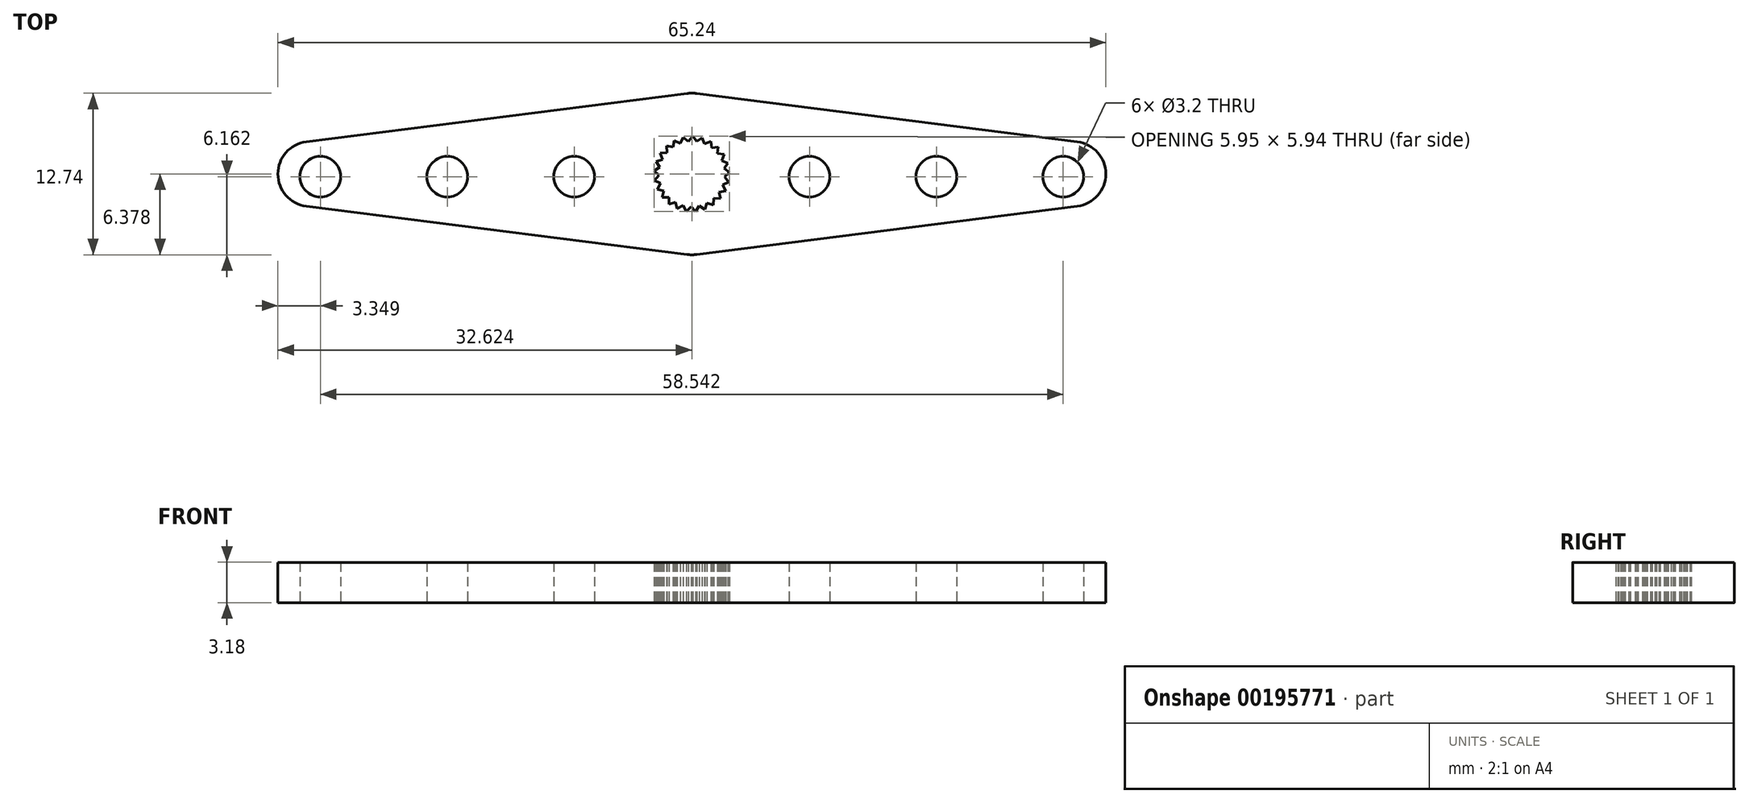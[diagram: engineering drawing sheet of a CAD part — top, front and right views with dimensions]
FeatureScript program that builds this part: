
annotation { "Feature Type Name" : "Feature", "Feature Type Description" : "" }
export const myFeature = defineFeature(function(context is Context, id is Id, definition is map)
    precondition{}
    {
        {
            var Q0;
            Q0=qCreatedBy(makeId("Top.planeOp"),FACE);
            var sketch = newSketch(context, id + "F0", { "sketchPlane" : qUnion([Q0])});
            skLineSegment(sketch, "E0", {"start": v(-2.48, 1.65) * mm, "end": v(-2.31, 1.15) * mm});
            skLineSegment(sketch, "E1", {"start": v(-2.31, 1.15) * mm, "end": v(-2.81, 0.98) * mm});
            skLineSegment(sketch, "E2.1.0", {"start": v(-2.81, 0.98) * mm, "end": v(-2.53, 0.54) * mm});
            skLineSegment(sketch, "E2.1.1", {"start": v(-2.53, 0.54) * mm, "end": v(-2.97, 0.25) * mm});
            skLineSegment(sketch, "E2.2.0", {"start": v(-2.97, 0.25) * mm, "end": v(-2.58, -0.1) * mm});
            skLineSegment(sketch, "E2.2.1", {"start": v(-2.58, -0.1) * mm, "end": v(-2.94, -0.5) * mm});
            skLineSegment(sketch, "E2.3.0", {"start": v(-2.94, -0.5) * mm, "end": v(-2.47, -0.74) * mm});
            skLineSegment(sketch, "E2.3.1", {"start": v(-2.47, -0.74) * mm, "end": v(-2.72, -1.2) * mm});
            skLineSegment(sketch, "E2.4.0", {"start": v(-2.72, -1.2) * mm, "end": v(-2.21, -1.34) * mm});
            skLineSegment(sketch, "E2.4.1", {"start": v(-2.21, -1.34) * mm, "end": v(-2.34, -1.85) * mm});
            skLineSegment(sketch, "E2.5.0", {"start": v(-2.34, -1.85) * mm, "end": v(-1.8, -1.84) * mm});
            skLineSegment(sketch, "E2.5.1", {"start": v(-1.8, -1.84) * mm, "end": v(-1.8, -2.37) * mm});
            skLineSegment(sketch, "E2.6.0", {"start": v(-1.8, -2.37) * mm, "end": v(-1.3, -2.24) * mm});
            skLineSegment(sketch, "E2.6.1", {"start": v(-1.3, -2.24) * mm, "end": v(-1.16, -2.75) * mm});
            skLineSegment(sketch, "E2.7.0", {"start": v(-1.16, -2.75) * mm, "end": v(-0.7, -2.49) * mm});
            skLineSegment(sketch, "E2.7.1", {"start": v(-0.7, -2.49) * mm, "end": v(-0.44, -2.95) * mm});
            skLineSegment(sketch, "E2.8.0", {"start": v(-0.44, -2.95) * mm, "end": v(-0.06, -2.58) * mm});
            skLineSegment(sketch, "E2.8.1", {"start": v(-0.06, -2.58) * mm, "end": v(0.3, -2.96) * mm});
            skLineSegment(sketch, "E2.9.0", {"start": v(0.3, -2.96) * mm, "end": v(0.59, -2.52) * mm});
            skLineSegment(sketch, "E2.9.1", {"start": v(0.59, -2.52) * mm, "end": v(1.04, -2.8) * mm});
            skLineSegment(sketch, "E2.10.0", {"start": v(1.04, -2.8) * mm, "end": v(1.2, -2.3) * mm});
            skLineSegment(sketch, "E2.10.1", {"start": v(1.2, -2.3) * mm, "end": v(1.7, -2.45) * mm});
            skLineSegment(sketch, "E2.11.0", {"start": v(1.7, -2.45) * mm, "end": v(1.73, -1.92) * mm});
            skLineSegment(sketch, "E2.11.1", {"start": v(1.73, -1.92) * mm, "end": v(2.25, -1.95) * mm});
            skLineSegment(sketch, "E2.12.0", {"start": v(2.25, -1.95) * mm, "end": v(2.15, -1.43) * mm});
            skLineSegment(sketch, "E2.12.1", {"start": v(2.15, -1.43) * mm, "end": v(2.67, -1.33) * mm});
            skLineSegment(sketch, "E2.13.0", {"start": v(2.67, -1.33) * mm, "end": v(2.44, -0.85) * mm});
            skLineSegment(sketch, "E2.13.1", {"start": v(2.44, -0.85) * mm, "end": v(2.91, -0.62) * mm});
            skLineSegment(sketch, "E2.14.0", {"start": v(2.91, -0.62) * mm, "end": v(2.57, -0.22) * mm});
            skLineSegment(sketch, "E2.14.1", {"start": v(2.57, -0.22) * mm, "end": v(2.98, 0.12) * mm});
            skLineSegment(sketch, "E2.15.0", {"start": v(2.98, 0.12) * mm, "end": v(2.55, 0.43) * mm});
            skLineSegment(sketch, "E2.15.1", {"start": v(2.55, 0.43) * mm, "end": v(2.85, 0.86) * mm});
            skLineSegment(sketch, "E2.16.0", {"start": v(2.85, 0.86) * mm, "end": v(2.36, 1.05) * mm});
            skLineSegment(sketch, "E2.16.1", {"start": v(2.36, 1.05) * mm, "end": v(2.55, 1.54) * mm});
            skLineSegment(sketch, "E2.17.0", {"start": v(2.55, 1.54) * mm, "end": v(2.03, 1.6) * mm});
            skLineSegment(sketch, "E2.17.1", {"start": v(2.03, 1.6) * mm, "end": v(2.09, 2.13) * mm});
            skLineSegment(sketch, "E2.18.0", {"start": v(2.09, 2.13) * mm, "end": v(1.56, 2.06) * mm});
            skLineSegment(sketch, "E2.18.1", {"start": v(1.56, 2.06) * mm, "end": v(1.5, 2.58) * mm});
            skLineSegment(sketch, "E2.19.0", {"start": v(1.5, 2.58) * mm, "end": v(1, 2.38) * mm});
            skLineSegment(sketch, "E2.19.1", {"start": v(1, 2.38) * mm, "end": v(0.8, 2.87) * mm});
            skLineSegment(sketch, "E2.20.0", {"start": v(0.8, 2.87) * mm, "end": v(0.38, 2.56) * mm});
            skLineSegment(sketch, "E2.20.1", {"start": v(0.38, 2.56) * mm, "end": v(0.07, 2.98) * mm});
            skLineSegment(sketch, "E2.21.0", {"start": v(0.07, 2.98) * mm, "end": v(-0.27, 2.57) * mm});
            skLineSegment(sketch, "E2.21.1", {"start": v(-0.27, 2.57) * mm, "end": v(-0.68, 2.9) * mm});
            skLineSegment(sketch, "E2.22.0", {"start": v(-0.68, 2.9) * mm, "end": v(-0.9, 2.42) * mm});
            skLineSegment(sketch, "E2.22.1", {"start": v(-0.9, 2.42) * mm, "end": v(-1.38, 2.64) * mm});
            skLineSegment(sketch, "E2.23.0", {"start": v(-1.38, 2.64) * mm, "end": v(-1.47, 2.12) * mm});
            skLineSegment(sketch, "E2.23.1", {"start": v(-1.47, 2.12) * mm, "end": v(-2, 2.22) * mm});
            skLineSegment(sketch, "E2.24.0", {"start": v(-2, 2.22) * mm, "end": v(-1.95, 1.69) * mm});
            skLineSegment(sketch, "E2.24.1", {"start": v(-1.95, 1.69) * mm, "end": v(-2.48, 1.65) * mm});
            skPoint(sketch, "E2.center", {"position": v(0, 0) * mm});
            skLineSegment(sketch, "E3", {"start": v(-0.38, 6.35) * mm, "end": v(-30.38, 2.54) * mm});
            skLineSegment(sketch, "E4", {"start": v(-0.38, -6.35) * mm, "end": v(-30.38, -2.54) * mm});
            skArc(sketch, "E5", {"start": v(-30.38, 2.54) * mm, "mid": v(-32.62, 0) * mm, "end": v(-30.38, -2.54) * mm});
            skCircle(sketch, "E6", {"center": v(-9.27, -0.2) * mm, "radius": 1.6 * mm});
            skCircle(sketch, "E7", {"center": v(-19.27, -0.2) * mm, "radius": 1.6 * mm});
            skCircle(sketch, "E8", {"center": v(-29.27, -0.2) * mm, "radius": 1.6 * mm});
            skLineSegment(sketch, "E9.MirrorCS", {"start": v(0.38, 6.35) * mm, "end": v(30.38, 2.54) * mm});
            skLineSegment(sketch, "E10.MirrorCS", {"start": v(0.38, -6.35) * mm, "end": v(30.38, -2.54) * mm});
            skCircle(sketch, "E11.MirrorC", {"center": v(9.27, -0.2) * mm, "radius": 1.6 * mm});
            skCircle(sketch, "E12.MirrorC", {"center": v(19.27, -0.2) * mm, "radius": 1.6 * mm});
            skCircle(sketch, "E13.MirrorC", {"center": v(29.27, -0.2) * mm, "radius": 1.6 * mm});
            skArc(sketch, "E14.MirrorCS", {"start": v(30.38, 2.54) * mm, "mid": v(32.62, 0) * mm, "end": v(30.38, -2.54) * mm});
            skArc(sketch, "E15", {"start": v(0.38, 6.35) * mm, "mid": v(0, 6.37) * mm, "end": v(-0.38, 6.35) * mm});
            skArc(sketch, "E16", {"start": v(-0.38, -6.35) * mm, "mid": v(0, -6.37) * mm, "end": v(0.38, -6.35) * mm});
            skSolve(sketch);
        }
        {
            var Q0;
            Q0=makeQuery(id+"F0.imprint","IMPRINT",FACE,{"disambiguationData":[TD([[makeQuery(id+"F0.imprint","IMPRINT",EDGE,{"derivedFrom":sQuery(id+"F0.wireOp",EDGE,"E0")}),-1.0]])]});
            extrude(context, id + "F1", {"entities" : qUnion([Q0]), "depth" : 3.17 * mm});
        }
    });
